# Revit family: Difusores abiertos para pared
name_source: partatom
category: Rociadores
revit_build: Autodesk Revit 2017 (Build: 20160225_1515(x64)
units: mm (PartAtom-declared; Revit-internal decimal feet)

## family parameters
Compartido = No
Corte con vacíos al cargar = No
Cota de conector redondo = Radio de uso
Mantener orientación de anotación = No
Número OmniClass = 23.65.70.17.11.24
Punto de cálculo de habitación = No
Se basa en plano de trabajo = Sí
Siempre vertical = Sí
Tipo de pieza = Normal
Título OmniClass = Fire Fighting Sprinkler Heads

## types (1)
- Difusor abierto 5 toberas 120º -  2,0 a 25,5 l/min
    120 = Sí
    Clase de presión = Norma
    Cobertura = Norma
    Descripción = Cabeza nebulizadora abierta para instalación en tubería seca, toberas montadas a 120º a un rango de caudales suficiente para cubrir una amplia gama de riesgos.
    Elevación por defecto = 1219 mm
    Fabricante = Aguilera Electrónica
    Flujo = 2.0 L/min
    Flujo máximo = 25.5 L/min
    Flujo mínimo = 2.0 L/min
    Modelo = AN/CAP120T5
    Orificio = Norma
    Respuesta = Norma
    Símbolo = Sí
    Símbolo texto modelo = Sí
    URL = http://aguilera.es
    Zona de acción = Sí
    Ángulo = 120.00°
